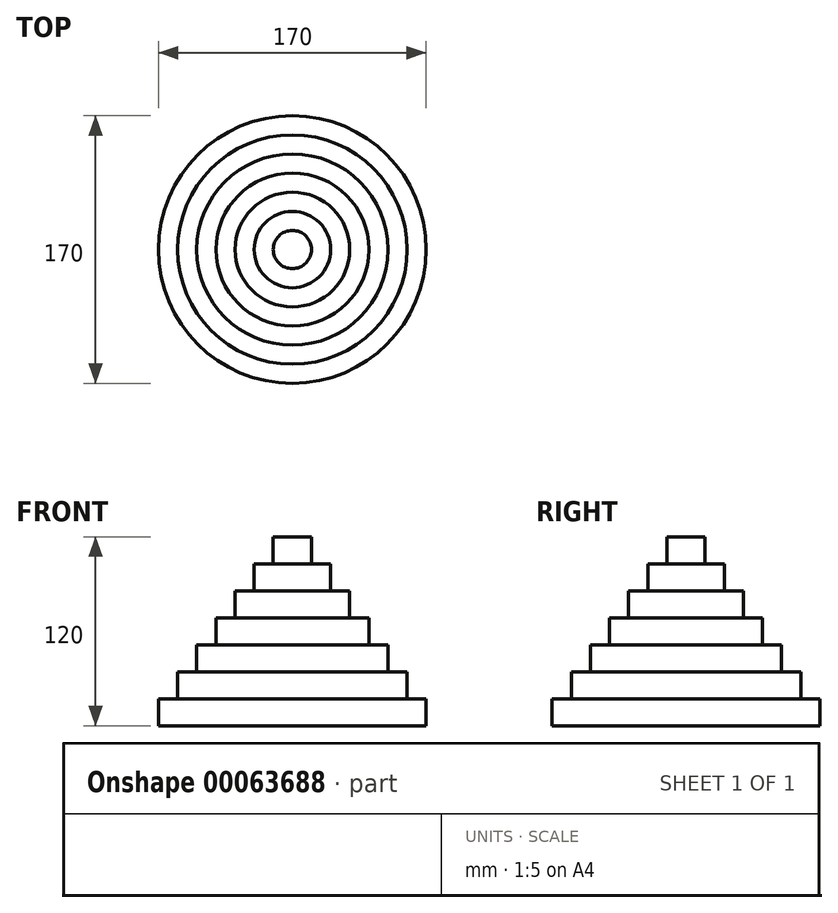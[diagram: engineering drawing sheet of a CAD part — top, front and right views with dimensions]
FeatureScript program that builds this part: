
annotation { "Feature Type Name" : "Feature", "Feature Type Description" : "" }
export const myFeature = defineFeature(function(context is Context, id is Id, definition is map)
    precondition{}
    {
        {
            var Q0;
            Q0=qCreatedBy(makeId("Front.planeOp"),FACE);
            var sketch = newSketch(context, id + "F0", { "sketchPlane" : qUnion([Q0])});
            skLineSegment(sketch, "E0", {"start": v(0, 0) * mm, "end": v(0, 120) * mm});
            skLineSegment(sketch, "E1", {"start": v(0, 120) * mm, "end": v(-85, 0) * mm, "construction": true});
            skLineSegment(sketch, "E2", {"start": v(-85, 0) * mm, "end": v(0, 0) * mm});
            skLineSegment(sketch, "E3", {"start": v(-85, 0) * mm, "end": v(-85, 17.14) * mm});
            skLineSegment(sketch, "E4", {"start": v(-85, 17.14) * mm, "end": v(-72.86, 17.14) * mm});
            skLineSegment(sketch, "E5", {"start": v(-72.86, 17.14) * mm, "end": v(-72.86, 34.29) * mm});
            skLineSegment(sketch, "E6", {"start": v(-72.86, 34.29) * mm, "end": v(-60.71, 34.29) * mm});
            skLineSegment(sketch, "E7", {"start": v(-60.71, 34.29) * mm, "end": v(-60.71, 51.43) * mm});
            skLineSegment(sketch, "E8", {"start": v(-60.71, 51.43) * mm, "end": v(-48.57, 51.43) * mm});
            skLineSegment(sketch, "E9", {"start": v(-48.57, 51.43) * mm, "end": v(-48.57, 68.57) * mm});
            skLineSegment(sketch, "E10", {"start": v(-48.57, 68.57) * mm, "end": v(-36.43, 68.57) * mm});
            skLineSegment(sketch, "E11", {"start": v(-36.43, 68.57) * mm, "end": v(-36.43, 85.71) * mm});
            skLineSegment(sketch, "E12", {"start": v(-36.43, 85.71) * mm, "end": v(-24.29, 85.71) * mm});
            skLineSegment(sketch, "E13", {"start": v(-24.29, 85.71) * mm, "end": v(-24.29, 102.86) * mm});
            skLineSegment(sketch, "E14", {"start": v(-24.29, 102.86) * mm, "end": v(-12.14, 102.86) * mm});
            skLineSegment(sketch, "E15", {"start": v(-12.14, 102.86) * mm, "end": v(-12.14, 120) * mm});
            skLineSegment(sketch, "E16", {"start": v(-12.14, 120) * mm, "end": v(0, 120) * mm});
            skSolve(sketch);
        }
        {
            var Q0;
            Q0=makeQuery(id+"F0.imprint","IMPRINT",FACE,{"disambiguationData":[TD([[makeQuery(id+"F0.imprint","IMPRINT",EDGE,{"derivedFrom":sQuery(id+"F0.wireOp",EDGE,"E0")}),1.0]])]});
            var Q1;
            Q1=sQuery(id+"F0.wireOp",EDGE,"E0");
            revolve(context, id + "F1", {"entities" : qUnion([Q0]), "axis" : qUnion([Q1]), "revolveType" : RevolveType.FULL});
        }
    });
